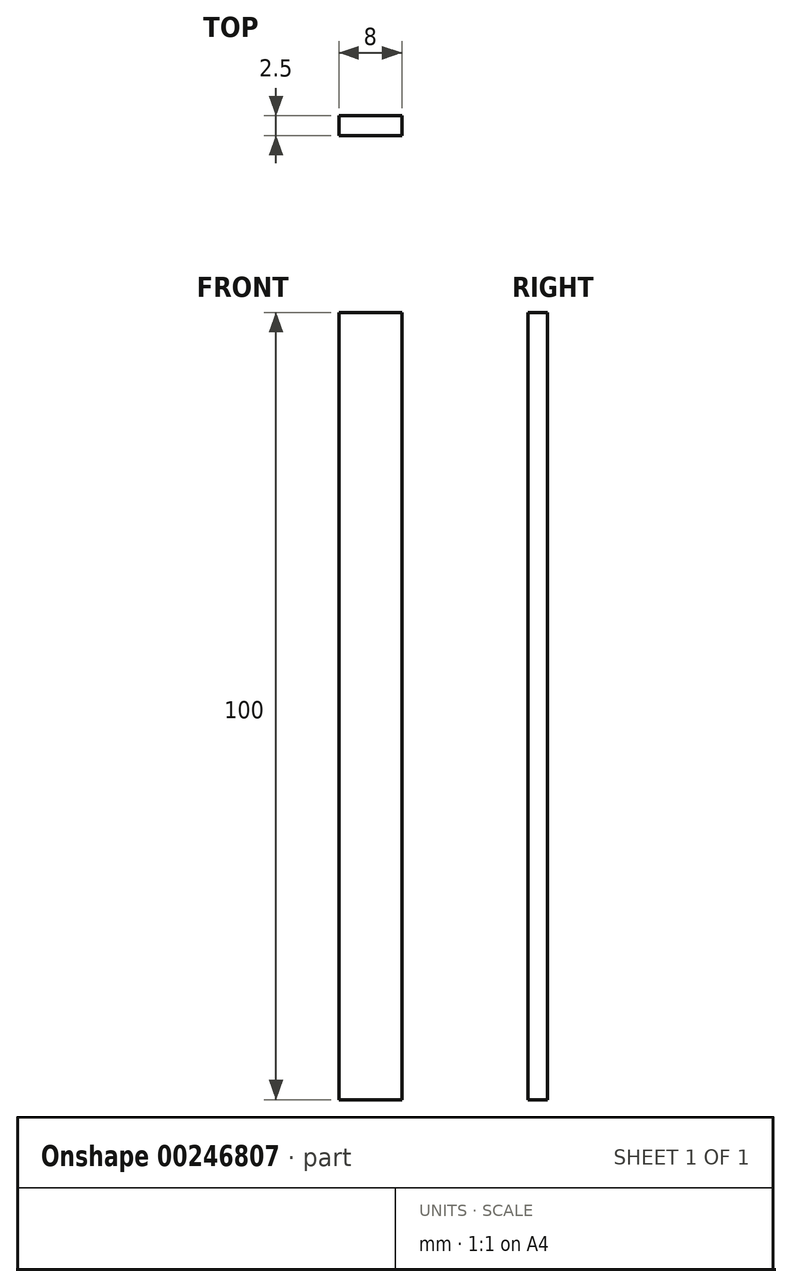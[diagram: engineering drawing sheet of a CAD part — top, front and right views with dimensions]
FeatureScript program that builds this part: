
annotation { "Feature Type Name" : "Feature", "Feature Type Description" : "" }
export const myFeature = defineFeature(function(context is Context, id is Id, definition is map)
    precondition{}
    {
        {
            var Q0;
            Q0=qCreatedBy(makeId("Top.planeOp"),FACE);
            var sketch = newSketch(context, id + "F0", { "sketchPlane" : qUnion([Q0])});
            skLineSegment(sketch, "E0.bottom", {"start": v(-1.88, 12.14) * mm, "end": v(6.12, 12.14) * mm});
            skLineSegment(sketch, "E0.top", {"start": v(-1.88, 9.64) * mm, "end": v(6.12, 9.64) * mm});
            skLineSegment(sketch, "E0.left", {"start": v(-1.88, 12.14) * mm, "end": v(-1.88, 9.64) * mm});
            skLineSegment(sketch, "E0.right", {"start": v(6.12, 12.14) * mm, "end": v(6.12, 9.64) * mm});
            skSolve(sketch);
        }
        {
            var Q0;
            Q0=makeQuery(id+"F0.imprint","IMPRINT",FACE,{"disambiguationData":[TD([[makeQuery(id+"F0.imprint","IMPRINT",EDGE,{"derivedFrom":sQuery(id+"F0.wireOp",EDGE,"E0.bottom")}),-1.0]])]});
            extrude(context, id + "F1", {"entities" : qUnion([Q0]), "depth" : 100 * mm});
        }
    });
